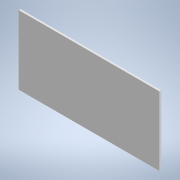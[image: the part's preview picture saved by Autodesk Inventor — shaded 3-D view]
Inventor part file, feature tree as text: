
AUTODESK INVENTOR PART (.ipt)
format: ipt  version: 2020 (Build 240168000, 168)  size: 88,576 bytes
history: native  units: mm
features: extrude x1, sketch x1
ambient origin geometry x8: Origin, YZ Plane, XZ Plane, XY Plane, X Axis, Y Axis, Z Axis, Center Point
bodies: Solid1 (feature_tree)
feature tree (2):
  extrude  "Extrusion1"  Depth=597.0mm
  sketch  "Sketch1"  dims[d0=1220.0mm d1=597.0mm d2=16.0mm d3=0.0mm d4=0.5mm d5=0.872665mm d6=0.5mm d7=0.872665mm]
